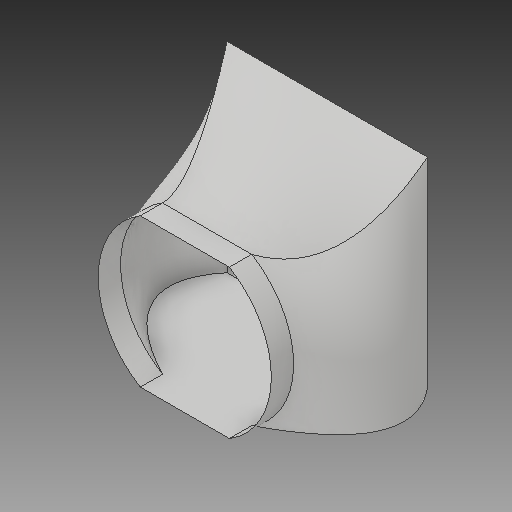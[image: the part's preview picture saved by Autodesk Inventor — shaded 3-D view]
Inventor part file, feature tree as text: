
AUTODESK INVENTOR PART (.ipt)
format: ipt  version: 2017 (Build 210142000, 142)  size: 323,584 bytes
history: native  units: in
note: dims shown in document units (in); Inventor stores cm internally (conversion verified against a paired STEP export)
features: extrude x2, other x2, sketch x2, loft x2, delete_face x1
ambient origin geometry x8: Origin, YZ Plane, XZ Plane, XY Plane, X Axis, Y Axis, Z Axis, Center Point
bodies: Solid1 (feature_tree)
feature tree (9):
  extrude  "connection"  Depth=2.7in
  other  "front half of room"
  other  "front of room"
  sketch  "Sketch3"  dims[d12=1.0in d13=0.0in d14=2.7in]
  loft  "shell make "
  loft  "shell cut"
  extrude  "connection to door"  Depth=1.0in
  delete_face  "Delete Face4"
  sketch  "Sketch5"  dims[d17=2.7in d26=69.0in d27=59.0in d33=1.0in d34=1.0in d35=1.0in d36=1.0in d153=6.21in d154=5.31in d157=0.0in d158=90.0deg d159=0.0in d160=90.0deg d161=0.0in d162=90.0deg d180=0.0in d181=90.0deg d182=0.0in d183=90.0deg d184=0.0in d185=90.0deg d217=3.082in d219=1.0in d220=1.0in d221=9.0in d222=9.0in d223=1.0in d245=1.0in d246=0.0in d262=4.0in d263=1.0in d264=4.8944in d266=3.8873in d267=3.8873in d271=1.6458in]
